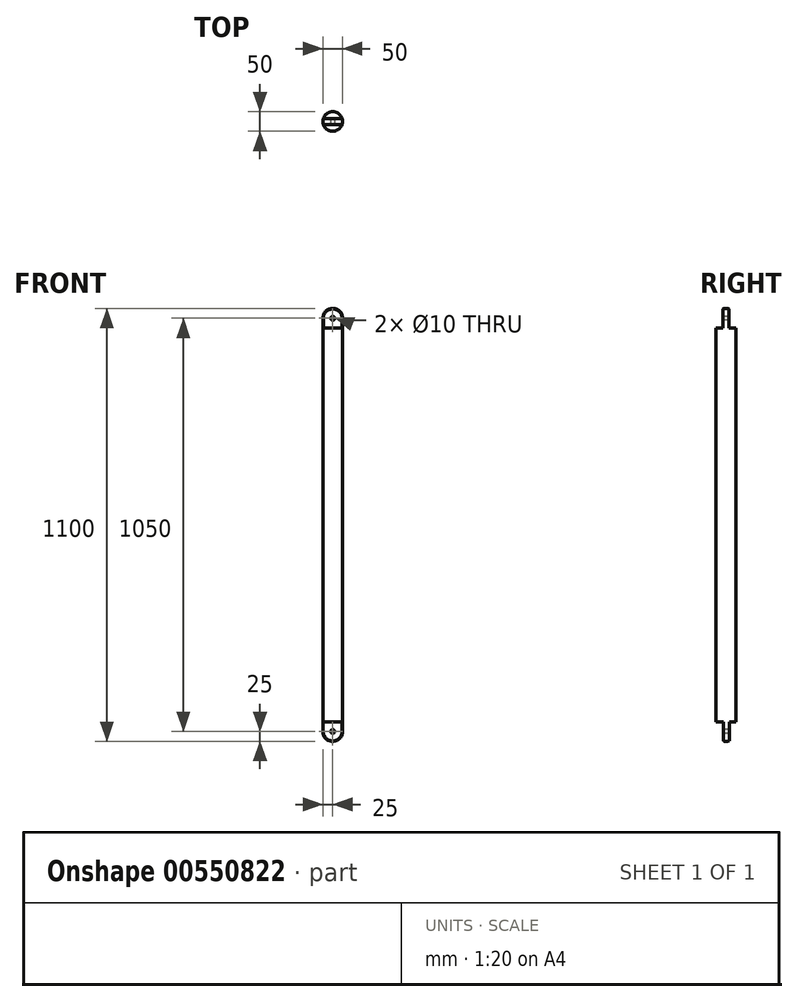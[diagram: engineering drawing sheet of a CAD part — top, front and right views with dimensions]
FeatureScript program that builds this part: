
annotation { "Feature Type Name" : "Feature", "Feature Type Description" : "" }
export const myFeature = defineFeature(function(context is Context, id is Id, definition is map)
    precondition{}
    {
        {
            var Q0;
            Q0=qCreatedBy(makeId("Top.planeOp"),FACE);
            var sketch = newSketch(context, id + "F0", { "sketchPlane" : qUnion([Q0])});
            skCircle(sketch, "E0", {"center": v(0, 0) * mm, "radius": 25 * mm});
            skSolve(sketch);
        }
        {
            var Q0;
            Q0=makeQuery(id+"F0.imprint","IMPRINT",FACE,{"disambiguationData":[TD([[makeQuery(id+"F0.imprint","IMPRINT",EDGE,{"derivedFrom":sQuery(id+"F0.wireOp",EDGE,"E0")}),1.0]])]});
            var Q1;
            Q1=sQuery(id+"F0.wireOp",EDGE,"E0");
            extrude(context, id + "F1", {"entities" : qUnion([Q0]), "surfaceEntities" : qUnion([Q1]), "depth" : 1000 * mm, "offsetDistance" : 25 * mm});
        }
        {
            var Q0;
            Q0=makeQuery(id+"F1.opExtrude","CAP_FACE",FACE,{"disambiguationData":[OSD([sQuery(id+"F0.wireOp",EDGE,"E0")])],"isStart":false});
            var sketch = newSketch(context, id + "F2", { "sketchPlane" : qUnion([Q0])});
            skLineSegment(sketch, "E1.bottom", {"start": v(25, -7.5) * mm, "end": v(-25, -7.5) * mm});
            skLineSegment(sketch, "E1.top", {"start": v(25, 7.5) * mm, "end": v(-25, 7.5) * mm});
            skLineSegment(sketch, "E1.left", {"start": v(25, -7.5) * mm, "end": v(25, 7.5) * mm});
            skLineSegment(sketch, "E1.right", {"start": v(-25, -7.5) * mm, "end": v(-25, 7.5) * mm});
            skPoint(sketch, "E1.middle", {"position": v(0, 0) * mm});
            skSolve(sketch);
        }
        {
            var Q0;
            {var subQ0=sQuery(id+"F2.wireOp",EDGE,"E1.bottom");var subQ1=makeQuery(id+"F1.opExtrude","CAP_EDGE",EDGE,{"disambiguationData":[OSD([sQuery(id+"F0.wireOp",EDGE,"E0")])],"isStart":false});var subQ4=makeQuery(id+"F2.imprint","INTERSECT",VERTEX,{"disambiguationData":[OD(0.0)],"derivedFrom":[subQ1,subQ0]});Q0=makeQuery(id+"F2.imprint","IMPRINT",FACE,{"disambiguationData":[TD([[makeQuery(id+"F2.imprint","IMPRINT",EDGE,{"disambiguationData":[TD([[subQ4,-1.0]])],"derivedFrom":subQ0}),-1.0]])]});}
            extrude(context, id + "F3", {"entities" : qUnion([Q0]), "operationType" : NewBodyOperationType.ADD, "depth" : 50 * mm, "offsetDistance" : 25 * mm});
        }
        {
            var Q0;
            {var subQ0=sQuery(id+"F0.wireOp",EDGE,"E0");var subQ1=makeQuery(id+"F1.opExtrude","CAP_EDGE",EDGE,{"disambiguationData":[OSD([subQ0])],"isStart":false});Q0=makeQuery(id+"F3.opExtrude","CAP_EDGE",EDGE,{"disambiguationData":[OSD([subQ0]),TDD([makeQuery(id+"F2.imprint","IMPRINT",EDGE,{"disambiguationData":[TD([[makeQuery(id+"F2.imprint","INTERSECT",VERTEX,{"disambiguationData":[OD(0.0)],"derivedFrom":[subQ1,sQuery(id+"F2.wireOp",EDGE,"E1.bottom")]}),-1.0]])],"derivedFrom":subQ1}),makeQuery(id+"F2.imprint","IMPRINT",EDGE,{"disambiguationData":[TD([[makeQuery(id+"F2.imprint","INTERSECT",VERTEX,{"disambiguationData":[OD(0.0)],"derivedFrom":[subQ1,sQuery(id+"F2.wireOp",EDGE,"E1.top")]}),1.0]])],"derivedFrom":subQ1})])],"isStart":false});}
            fillet(context, id + "F4", {"entities" : qUnion([Q0]), "radius" : 25 * mm, "tangentPropagation" : true, "allowEdgeOverflow" : false});
        }
        {
            var Q0;
            Q0=makeQuery(id+"F3.opExtrude","SWEPT_FACE",FACE,{"disambiguationData":[OSD([sQuery(id+"F2.wireOp",EDGE,"E1.bottom")])]});
            var sketch = newSketch(context, id + "F5", { "sketchPlane" : qUnion([Q0])});
            skCircle(sketch, "E2", {"center": v(0, 1025) * mm, "radius": 5 * mm});
            skSolve(sketch);
        }
        {
            var Q0;
            Q0=makeQuery(id+"F5.imprint","IMPRINT",FACE,{"disambiguationData":[TD([[makeQuery(id+"F5.imprint","IMPRINT",EDGE,{"derivedFrom":sQuery(id+"F5.wireOp",EDGE,"E2")}),1.0]])]});
            extrude(context, id + "F6", {"entities" : qUnion([Q0]), "operationType" : NewBodyOperationType.REMOVE, "oppositeDirection" : true, "depth" : 15 * mm, "offsetDistance" : 25 * mm});
        }
        {
            var Q0;
            Q0=makeQuery(id+"F1.opExtrude","CAP_FACE",FACE,{"disambiguationData":[OSD([sQuery(id+"F0.wireOp",EDGE,"E0")])],"isStart":true});
            var sketch = newSketch(context, id + "F7", { "sketchPlane" : qUnion([Q0])});
            skLineSegment(sketch, "E3.bottom", {"start": v(25, 6.7) * mm, "end": v(-25, 6.7) * mm});
            skLineSegment(sketch, "E3.top", {"start": v(25, -8.3) * mm, "end": v(-25, -8.3) * mm});
            skLineSegment(sketch, "E3.left", {"start": v(25, 6.7) * mm, "end": v(25, -8.3) * mm});
            skLineSegment(sketch, "E3.right", {"start": v(-25, 6.7) * mm, "end": v(-25, -8.3) * mm});
            skPoint(sketch, "E3.middle", {"position": v(0, -0.8) * mm});
            skSolve(sketch);
        }
        {
            var Q0;
            {var subQ0=sQuery(id+"F7.wireOp",EDGE,"E3.bottom");var subQ1=makeQuery(id+"F1.opExtrude","CAP_EDGE",EDGE,{"disambiguationData":[OSD([sQuery(id+"F0.wireOp",EDGE,"E0")])],"isStart":true});var subQ4=makeQuery(id+"F7.imprint","INTERSECT",VERTEX,{"disambiguationData":[OD(0.0)],"derivedFrom":[subQ1,subQ0]});Q0=makeQuery(id+"F7.imprint","IMPRINT",FACE,{"disambiguationData":[TD([[makeQuery(id+"F7.imprint","IMPRINT",EDGE,{"disambiguationData":[TD([[subQ4,-1.0]])],"derivedFrom":subQ0}),1.0]])]});}
            extrude(context, id + "F8", {"entities" : qUnion([Q0]), "operationType" : NewBodyOperationType.ADD, "depth" : 50 * mm, "offsetDistance" : 25 * mm});
        }
        {
            var Q0;
            {var subQ0=sQuery(id+"F0.wireOp",EDGE,"E0");var subQ1=makeQuery(id+"F1.opExtrude","CAP_EDGE",EDGE,{"disambiguationData":[OSD([subQ0])],"isStart":true});Q0=makeQuery(id+"F8.opExtrude","CAP_EDGE",EDGE,{"disambiguationData":[OSD([subQ0]),TDD([makeQuery(id+"F7.imprint","IMPRINT",EDGE,{"disambiguationData":[TD([[makeQuery(id+"F7.imprint","INTERSECT",VERTEX,{"disambiguationData":[OD(0.0)],"derivedFrom":[subQ1,sQuery(id+"F7.wireOp",EDGE,"E3.bottom")]}),-1.0]])],"derivedFrom":subQ1}),makeQuery(id+"F7.imprint","IMPRINT",EDGE,{"disambiguationData":[TD([[makeQuery(id+"F7.imprint","INTERSECT",VERTEX,{"disambiguationData":[OD(0.0)],"derivedFrom":[subQ1,sQuery(id+"F7.wireOp",EDGE,"E3.top")]}),1.0]])],"derivedFrom":subQ1})])],"isStart":false});}
            fillet(context, id + "F9", {"entities" : qUnion([Q0]), "radius" : 25 * mm, "tangentPropagation" : true, "allowEdgeOverflow" : false});
        }
        {
            var Q0;
            Q0=makeQuery(id+"F8.opExtrude","SWEPT_FACE",FACE,{"disambiguationData":[OSD([sQuery(id+"F7.wireOp",EDGE,"E3.bottom")])]});
            var sketch = newSketch(context, id + "F10", { "sketchPlane" : qUnion([Q0])});
            skCircle(sketch, "E4", {"center": v(0, -25) * mm, "radius": 5 * mm});
            skSolve(sketch);
        }
        {
            var Q0;
            Q0=makeQuery(id+"F10.imprint","IMPRINT",FACE,{"disambiguationData":[TD([[makeQuery(id+"F10.imprint","IMPRINT",EDGE,{"derivedFrom":sQuery(id+"F10.wireOp",EDGE,"E4")}),1.0]])]});
            extrude(context, id + "F11", {"entities" : qUnion([Q0]), "operationType" : NewBodyOperationType.REMOVE, "oppositeDirection" : true, "depth" : 15 * mm, "offsetDistance" : 25 * mm});
        }
    });
